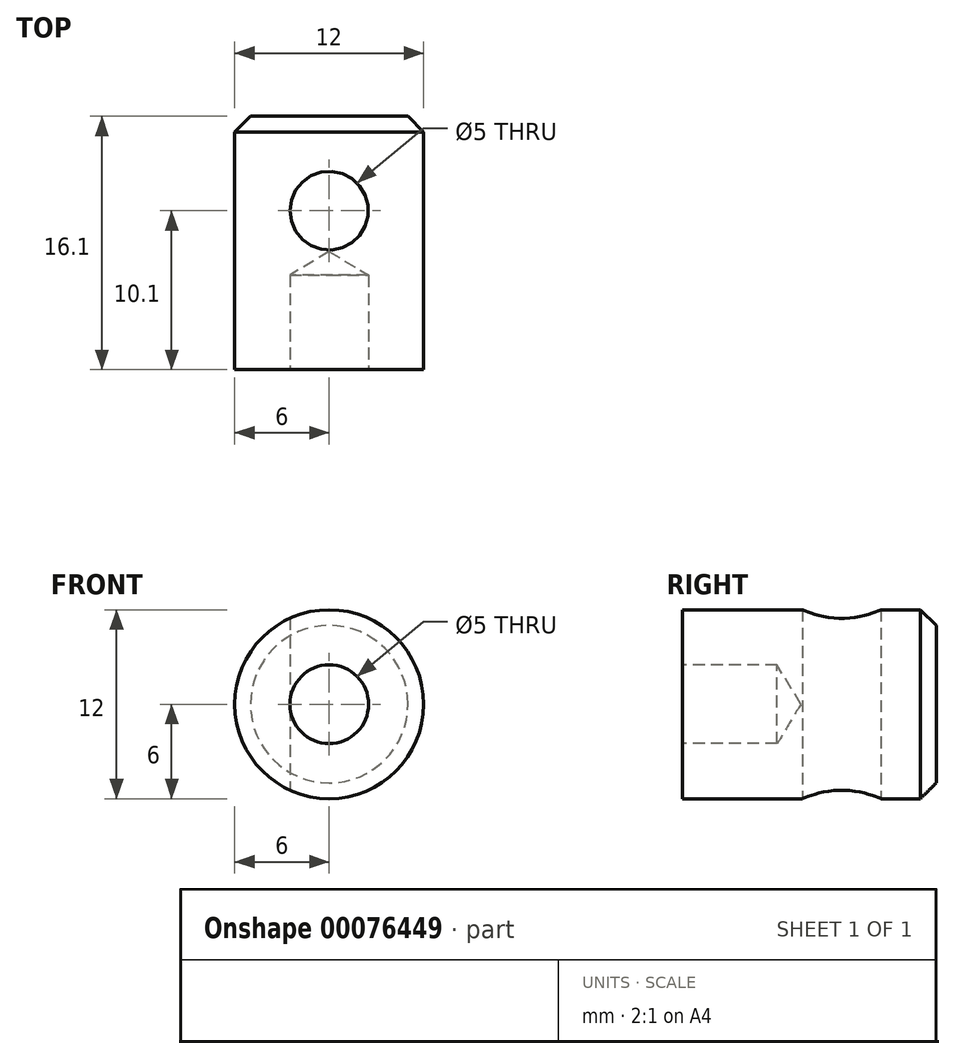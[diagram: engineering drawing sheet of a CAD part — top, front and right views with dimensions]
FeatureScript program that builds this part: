
annotation { "Feature Type Name" : "Feature", "Feature Type Description" : "" }
export const myFeature = defineFeature(function(context is Context, id is Id, definition is map)
    precondition{}
    {
        {
            var Q0;
            Q0=qCreatedBy(makeId("Front.planeOp"),FACE);
            var sketch = newSketch(context, id + "F0", { "sketchPlane" : qUnion([Q0])});
            skCircle(sketch, "E0", {"center": v(0, 0) * mm, "radius": 6 * mm});
            skSolve(sketch);
        }
        {
            var Q0;
            Q0=makeQuery(id+"F0.imprint","IMPRINT",FACE,{"disambiguationData":[TD([[makeQuery(id+"F0.imprint","IMPRINT",EDGE,{"derivedFrom":sQuery(id+"F0.wireOp",EDGE,"E0")}),1.0]])]});
            extrude(context, id + "F1", {"entities" : qUnion([Q0]), "flatOperationType" : FlatOperationType.REMOVE, "oppositeDirection" : true, "offsetDistance" : 25 * mm, "depth" : 16.1 * mm, "domain" : OperationDomain.MODEL});
        }
        {
            var Q0;
            Q0=sQuery(id+"F0.wireOp",VERTEX,"E0.center");
            var Q1;
            Q1=makeQuery(id+"F1.opExtrude","SWEPT_BODY",BODY,{"disambiguationData":[OSD([sQuery(id+"F0.wireOp",EDGE,"E0")])]});
            hole(context, id + "F2", {"style" : HoleStyle.SIMPLE, "endStyle" : HoleEndStyle.BLIND, "standardTappedOrClearance" : lookupTablePath({ "standard" : "ISO", "engagement" : "75%", "pitch" : "1 mm", "size" : "M6", "type" : "Tapped" }), "standardBlindInLast" : lookupTablePath({ "standard" : "ISO", "engagement" : "75%", "pitch" : "1 mm", "size" : "M6", "type" : "Tapped" }), "holeDiameter" : 5 * mm, "holeDepth" : 6 * mm, "locations" : qUnion([Q0]), "scope" : qUnion([Q1]), "majorDiameter" : 6 * mm});
        }
        {
            var Q0;
            Q0=qCreatedBy(makeId("Top.planeOp"),FACE);
            var sketch = newSketch(context, id + "F3", { "sketchPlane" : qUnion([Q0])});
            skCircle(sketch, "E1", {"center": v(0, 10.1) * mm, "radius": 2.5 * mm});
            skSolve(sketch);
        }
        {
            var Q0;
            Q0 = qSketchRegion(id + "F3", true);
            extrude(context, id + "F4", {"entities" : qUnion([Q0]), "operationType" : NewBodyOperationType.REMOVE, "depth" : 14 * mm, "symmetric" : true});
        }
        {
            var Q0;
            Q0=makeQuery(id+"F1.opExtrude","CAP_EDGE",EDGE,{"disambiguationData":[OSD([sQuery(id+"F0.wireOp",EDGE,"E0")])],"isStart":false});
            chamfer(context, id + "F5", {"entities" : qUnion([Q0]), "width" : 1 * mm, "tangentPropagation" : true});
        }
    });
